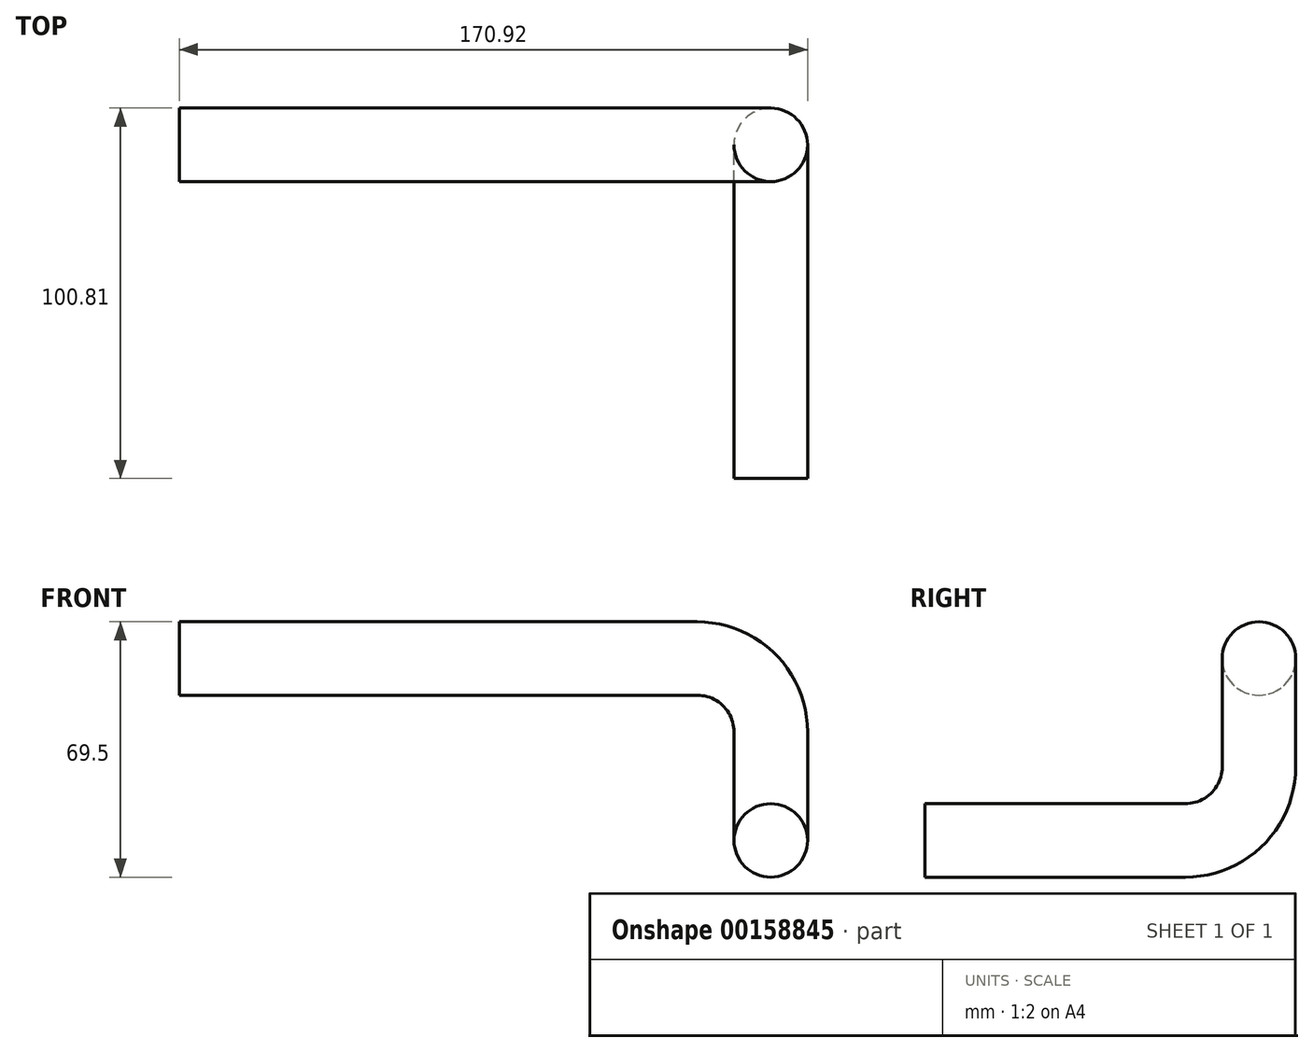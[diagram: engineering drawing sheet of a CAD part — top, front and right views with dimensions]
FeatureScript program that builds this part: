
annotation { "Feature Type Name" : "Feature", "Feature Type Description" : "" }
export const myFeature = defineFeature(function(context is Context, id is Id, definition is map)
    precondition{}
    {
        {
            var Q0;
            Q0=qCreatedBy(makeId("Right.planeOp"),FACE);
            var sketch = newSketch(context, id + "F0", { "sketchPlane" : qUnion([Q0])});
            skLineSegment(sketch, "E0", {"start": v(0, 0) * mm, "end": v(70.81, 0) * mm});
            skLineSegment(sketch, "E1", {"start": v(90.81, 20) * mm, "end": v(90.81, 29.5) * mm});
            skPoint(sketch, "E2.visualSharp", {"position": v(90.81, 0) * mm});
            skArc(sketch, "E2.filletArc", {"start": v(70.81, 0) * mm, "mid": v(84.95, 5.86) * mm, "end": v(90.81, 20) * mm});
            skSolve(sketch);
        }
        {
            var Q0;
            Q0=qCreatedBy(makeId("Front.planeOp"),FACE);
            cPlane(context, id + "F1", {"entities" : qUnion([Q0]), "cplaneType" : CPlaneType.OFFSET, "offset" : 90.81 * mm, "oppositeDirection" : true, "width" : 150 * mm, "height" : 150 * mm});
        }
        {
            var Q0;
            Q0=qCreatedBy(id+"F1.planeOp",FACE);
            var sketch = newSketch(context, id + "F2", { "sketchPlane" : qUnion([Q0])});
            skLineSegment(sketch, "E3", {"start": v(-20, 49.5) * mm, "end": v(-160.92, 49.5) * mm});
            skLineSegment(sketch, "E4", {"start": v(0, 29.5) * mm, "end": v(0, -19.87) * mm});
            skPoint(sketch, "E5.visualSharp", {"position": v(0, 49.5) * mm});
            skArc(sketch, "E5.filletArc", {"start": v(0, 29.5) * mm, "mid": v(-5.86, 43.64) * mm, "end": v(-20, 49.5) * mm});
            skSolve(sketch);
        }
        {
            var Q0;
            Q0=qCreatedBy(makeId("Front.planeOp"),FACE);
            var sketch = newSketch(context, id + "F3", { "sketchPlane" : qUnion([Q0])});
            skCircle(sketch, "E6", {"center": v(0, 0) * mm, "radius": 10 * mm});
            skSolve(sketch);
        }
        {
            var Q0;
            Q0=makeQuery(id+"F3.imprint","IMPRINT",FACE,{"disambiguationData":[TD([[makeQuery(id+"F3.imprint","IMPRINT",EDGE,{"derivedFrom":sQuery(id+"F3.wireOp",EDGE,"E6")}),1.0]])]});
            var Q1;
            Q1=sQuery(id+"F0.wireOp",EDGE,"E0");
            var Q2;
            Q2=sQuery(id+"F0.wireOp",EDGE,"E1");
            var Q3;
            Q3=sQuery(id+"F2.wireOp",EDGE,"E3");
            var Q4;
            Q4=sQuery(id+"F0.wireOp",EDGE,"E2.filletArc");
            var Q5;
            Q5=sQuery(id+"F2.wireOp",EDGE,"E5.filletArc");
            sweep(context, id + "F4", {"profiles" : qUnion([Q0]), "path" : qUnion([Q1, Q2, Q3, Q4, Q5])});
        }
    });
